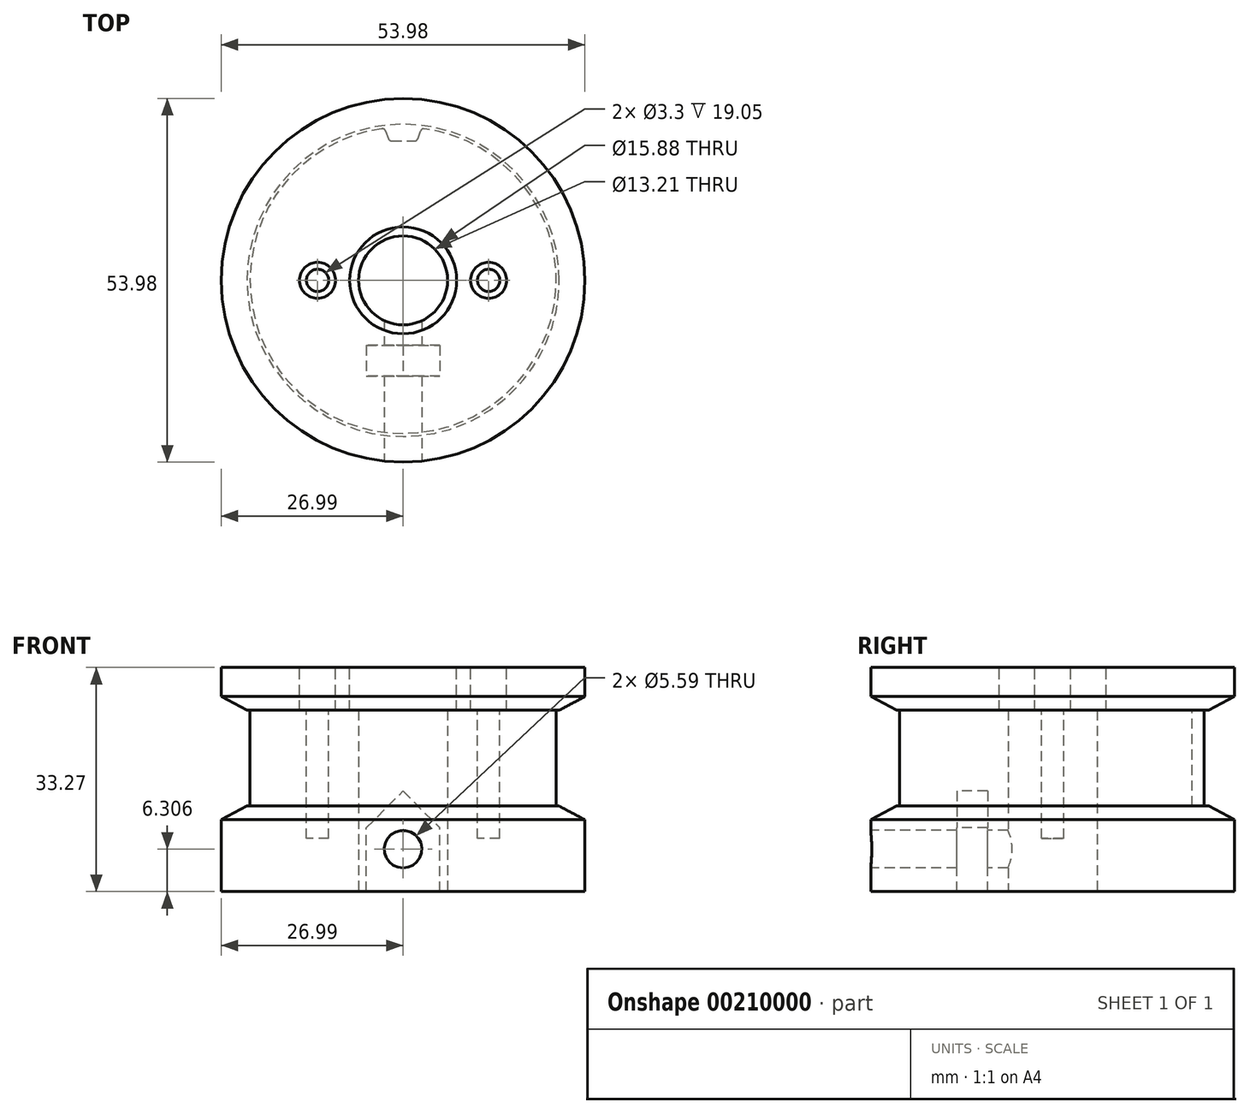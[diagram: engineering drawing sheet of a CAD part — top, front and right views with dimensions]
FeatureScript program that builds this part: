
annotation { "Feature Type Name" : "Feature", "Feature Type Description" : "" }
export const myFeature = defineFeature(function(context is Context, id is Id, definition is map)
    precondition{}
    {
        {
            var Q0;
            Q0=qCreatedBy(makeId("Top.planeOp"),FACE);
            var sketch = newSketch(context, id + "F0", { "sketchPlane" : qUnion([Q0])});
            skCircle(sketch, "E0", {"center": v(0, 0) * mm, "radius": 26.99 * mm});
            skSolve(sketch);
        }
        {
            var Q0;
            Q0 = qSketchRegion(id + "F0", true);
            extrude(context, id + "F1", {"entities" : qUnion([Q0]), "depth" : 12.7 * mm});
        }
        {
            var Q0;
            Q0=makeQuery(id+"F1.opExtrude","CAP_FACE",FACE,{"disambiguationData":[OSD([sQuery(id+"F0.wireOp",EDGE,"E0")])],"isStart":false});
            var sketch = newSketch(context, id + "F2", { "sketchPlane" : qUnion([Q0])});
            skCircle(sketch, "E1", {"center": v(0, 0) * mm, "radius": 22.73 * mm});
            skSolve(sketch);
        }
        {
            var Q0;
            Q0 = qSketchRegion(id + "F2", true);
            extrude(context, id + "F3", {"entities" : qUnion([Q0]), "operationType" : NewBodyOperationType.ADD, "depth" : 14.22 * mm});
        }
        {
            var Q0;
            Q0=makeQuery(id+"F3.opExtrude","CAP_FACE",FACE,{"disambiguationData":[OSD([sQuery(id+"F2.wireOp",EDGE,"E1")])],"isStart":false});
            var sketch = newSketch(context, id + "F4", { "sketchPlane" : qUnion([Q0])});
            skArc(sketch, "E2", {"start": v(-3.16, 22.51) * mm, "mid": v(0, 22.73) * mm, "end": v(3.16, 22.51) * mm});
            skArc(sketch, "E3", {"start": v(-3.16, 22.51) * mm, "mid": v(-2.83, 22.44) * mm, "end": v(-2.6, 22.18) * mm});
            skArc(sketch, "E4", {"start": v(3.16, 22.51) * mm, "mid": v(2.83, 22.44) * mm, "end": v(2.6, 22.18) * mm});
            skLineSegment(sketch, "E5", {"start": v(0, 0) * mm, "end": v(-3.16, 22.51) * mm, "construction": true});
            skLineSegment(sketch, "E6", {"start": v(3.16, 22.51) * mm, "end": v(0, 0) * mm, "construction": true});
            skLineSegment(sketch, "E7", {"start": v(-2.6, 22.18) * mm, "end": v(-2.2, 21.04) * mm});
            skLineSegment(sketch, "E8", {"start": v(-1.71, 20.7) * mm, "end": v(1.71, 20.7) * mm});
            skLineSegment(sketch, "E9", {"start": v(2.2, 21.04) * mm, "end": v(2.6, 22.18) * mm});
            skPoint(sketch, "E10.visualSharp", {"position": v(2.07, 20.7) * mm});
            skArc(sketch, "E10.filletArc", {"start": v(1.71, 20.7) * mm, "mid": v(2, 20.8) * mm, "end": v(2.2, 21.04) * mm});
            skPoint(sketch, "E11.visualSharp", {"position": v(-2.07, 20.7) * mm});
            skArc(sketch, "E11.filletArc", {"start": v(-2.2, 21.04) * mm, "mid": v(-2, 20.8) * mm, "end": v(-1.71, 20.7) * mm});
            skLineSegment(sketch, "E12", {"start": v(0, 0) * mm, "end": v(0, 22.73) * mm, "construction": true});
            skSolve(sketch);
        }
        {
            var Q0;
            Q0 = qSketchRegion(id + "F4", true);
            var Q1;
            Q1=makeQuery(id+"F1.opExtrude","CAP_FACE",FACE,{"disambiguationData":[OSD([sQuery(id+"F0.wireOp",EDGE,"E0")])],"isStart":false});
            extrude(context, id + "F5", {"entities" : qUnion([Q0]), "operationType" : NewBodyOperationType.REMOVE, "endBound" : BoundingType.UP_TO_SURFACE, "oppositeDirection" : true, "endBoundEntityFace" : qUnion([Q1]), "depth" : 25.4 * mm});
        }
        {
            var Q0;
            Q0=qCreatedBy(makeId("Right.planeOp"),FACE);
            var sketch = newSketch(context, id + "F6", { "sketchPlane" : qUnion([Q0])});
            skLineSegment(sketch, "E13", {"start": v(0, 0) * mm, "end": v(0, 71.38) * mm});
            skSolve(sketch);
        }
        {
            var Q0;
            Q0=makeQuery(id+"F1.opExtrude","CAP_FACE",FACE,{"disambiguationData":[OSD([sQuery(id+"F0.wireOp",EDGE,"E0")])],"isStart":true});
            var sketch = newSketch(context, id + "F7", { "sketchPlane" : qUnion([Q0])});
            skCircle(sketch, "E14", {"center": v(0, 0) * mm, "radius": 6.6 * mm});
            skSolve(sketch);
        }
        {
            var Q0;
            Q0 = qSketchRegion(id + "F7", true);
            extrude(context, id + "F8", {"entities" : qUnion([Q0]), "operationType" : NewBodyOperationType.REMOVE, "endBound" : BoundingType.THROUGH_ALL, "oppositeDirection" : true, "depth" : 25.4 * mm});
        }
        {
            var Q0;
            Q0=makeQuery(id+"F3.opExtrude","CAP_FACE",FACE,{"disambiguationData":[OSD([sQuery(id+"F2.wireOp",EDGE,"E1")])],"isStart":false});
            var sketch = newSketch(context, id + "F9", { "sketchPlane" : qUnion([Q0])});
            skCircle(sketch, "E15", {"center": v(-12.7, 0) * mm, "radius": 1.65 * mm});
            skCircle(sketch, "E16", {"center": v(12.7, 0) * mm, "radius": 1.65 * mm});
            skSolve(sketch);
        }
        {
            var Q0;
            Q0 = qSketchRegion(id + "F9", true);
            extrude(context, id + "F10", {"entities" : qUnion([Q0]), "operationType" : NewBodyOperationType.REMOVE, "oppositeDirection" : true, "depth" : 19.05 * mm});
        }
        {
            var Q0;
            Q0=qCreatedBy(makeId("Front.planeOp"),FACE);
            cPlane(context, id + "F11", {"entities" : qUnion([Q0]), "cplaneType" : CPlaneType.OFFSET, "offset" : 14.22 * mm, "width" : 152.4 * mm, "height" : 152.4 * mm});
        }
        {
            var Q0;
            Q0=qCreatedBy(id+"F11.planeOp",FACE);
            var sketch = newSketch(context, id + "F12", { "sketchPlane" : qUnion([Q0])});
            skLineSegment(sketch, "E17", {"start": v(5.46, 0) * mm, "end": v(-5.46, 0) * mm});
            skLineSegment(sketch, "E18", {"start": v(-5.46, 9.46) * mm, "end": v(0, 14.92) * mm});
            skLineSegment(sketch, "E19", {"start": v(0, 14.92) * mm, "end": v(5.46, 9.46) * mm});
            skLineSegment(sketch, "E20", {"start": v(0, 0) * mm, "end": v(-5.46, 3.15) * mm, "construction": true});
            skLineSegment(sketch, "E21", {"start": v(0, 0) * mm, "end": v(5.46, 3.15) * mm, "construction": true});
            skLineSegment(sketch, "E22", {"start": v(-5.46, 3.15) * mm, "end": v(-5.46, 9.46) * mm});
            skLineSegment(sketch, "E23", {"start": v(-5.46, 3.15) * mm, "end": v(-5.46, 0) * mm});
            skLineSegment(sketch, "E24", {"start": v(5.46, 0) * mm, "end": v(5.46, 3.15) * mm});
            skLineSegment(sketch, "E25", {"start": v(5.46, 3.15) * mm, "end": v(5.46, 9.46) * mm});
            skSolve(sketch);
        }
        {
            var Q0;
            Q0 = qSketchRegion(id + "F12", true);
            extrude(context, id + "F13", {"entities" : qUnion([Q0]), "operationType" : NewBodyOperationType.REMOVE, "oppositeDirection" : true, "depth" : 4.57 * mm});
        }
        {
            var Q0;
            Q0=makeQuery(id+"F13.boolean.opBoolean","COPY",FACE,{"derivedFrom":makeQuery(id+"F13.opExtrude","CAP_FACE",FACE,{"disambiguationData":[OSD([sQuery(id+"F12.wireOp",EDGE,"E17"),sQuery(id+"F12.wireOp",EDGE,"E18"),sQuery(id+"F12.wireOp",EDGE,"E19"),sQuery(id+"F12.wireOp",EDGE,"E22"),sQuery(id+"F12.wireOp",EDGE,"E23"),sQuery(id+"F12.wireOp",EDGE,"E24"),sQuery(id+"F12.wireOp",EDGE,"E25")])],"isStart":false})});
            var sketch = newSketch(context, id + "F14", { "sketchPlane" : qUnion([Q0])});
            skLineSegment(sketch, "E26", {"start": v(0, 0) * mm, "end": v(-5.46, 3.15) * mm, "construction": true});
            skLineSegment(sketch, "E27", {"start": v(-5.46, 3.15) * mm, "end": v(0, 6.3) * mm, "construction": true});
            skCircle(sketch, "E28", {"center": v(0, 6.3) * mm, "radius": 2.8 * mm});
            skSolve(sketch);
        }
        {
            var Q0;
            Q0 = qSketchRegion(id + "F14", true);
            var Q1;
            Q1=qCreatedBy(makeId("Front.planeOp"),FACE);
            extrude(context, id + "F15", {"entities" : qUnion([Q0]), "operationType" : NewBodyOperationType.REMOVE, "endBound" : BoundingType.UP_TO_SURFACE, "oppositeDirection" : true, "endBoundEntityFace" : qUnion([Q1]), "depth" : 25.4 * mm, "hasSecondDirection" : true, "secondDirectionOppositeDirection" : false, "secondDirectionDepth" : 25.4 * mm});
        }
        {
            var Q0;
            Q0=makeQuery(id+"F1.opExtrude","CAP_EDGE",EDGE,{"disambiguationData":[OSD([sQuery(id+"F0.wireOp",EDGE,"E0")])],"isStart":false});
            chamfer(context, id + "F16", {"entities" : qUnion([Q0]), "chamferType" : ChamferType.TWO_OFFSETS, "width1" : 3.8 * mm, "oppositeDirection" : false, "width2" : 2.03 * mm, "tangentPropagation" : true});
        }
        {
            var Q0;
            Q0=makeQuery(id+"F3.opExtrude","CAP_FACE",FACE,{"disambiguationData":[OSD([sQuery(id+"F2.wireOp",EDGE,"E1")])],"isStart":false});
            cPlane(context, id + "F17", {"entities" : qUnion([Q0]), "cplaneType" : CPlaneType.OFFSET, "offset" : 6.35 * mm, "width" : 152.4 * mm, "height" : 152.4 * mm});
        }
        {
            var Q0;
            Q0=qCreatedBy(id+"F17.planeOp",FACE);
            var sketch = newSketch(context, id + "F18", { "sketchPlane" : qUnion([Q0])});
            skCircle(sketch, "E29", {"center": v(0, 0) * mm, "radius": 26.99 * mm});
            skCircle(sketch, "E30", {"center": v(0, 0) * mm, "radius": 7.94 * mm});
            skCircle(sketch, "E31", {"center": v(-12.7, 0) * mm, "radius": 2.67 * mm});
            skCircle(sketch, "E32", {"center": v(12.7, 0) * mm, "radius": 2.67 * mm});
            skSolve(sketch);
        }
        {
            var Q0;
            Q0=makeQuery(id+"F18.imprint","IMPRINT",FACE,{"disambiguationData":[TD([[makeQuery(id+"F18.imprint","IMPRINT",EDGE,{"derivedFrom":sQuery(id+"F18.wireOp",EDGE,"E29")}),1.0]])]});
            var Q1;
            Q1=makeQuery(id+"F3.opExtrude","CAP_FACE",FACE,{"disambiguationData":[OSD([sQuery(id+"F2.wireOp",EDGE,"E1")])],"isStart":false});
            extrude(context, id + "F19", {"entities" : qUnion([Q0]), "endBound" : BoundingType.UP_TO_SURFACE, "oppositeDirection" : true, "endBoundEntityFace" : qUnion([Q1]), "depth" : 25.4 * mm});
        }
        {
            var Q0;
            Q0=makeQuery(id+"F19.opExtrude","CAP_EDGE",EDGE,{"disambiguationData":[OSD([sQuery(id+"F18.wireOp",EDGE,"E29")])],"isStart":false});
            chamfer(context, id + "F20", {"entities" : qUnion([Q0]), "chamferType" : ChamferType.TWO_OFFSETS, "width1" : 3.8 * mm, "oppositeDirection" : false, "width2" : 2.03 * mm, "tangentPropagation" : true});
        }
    });
